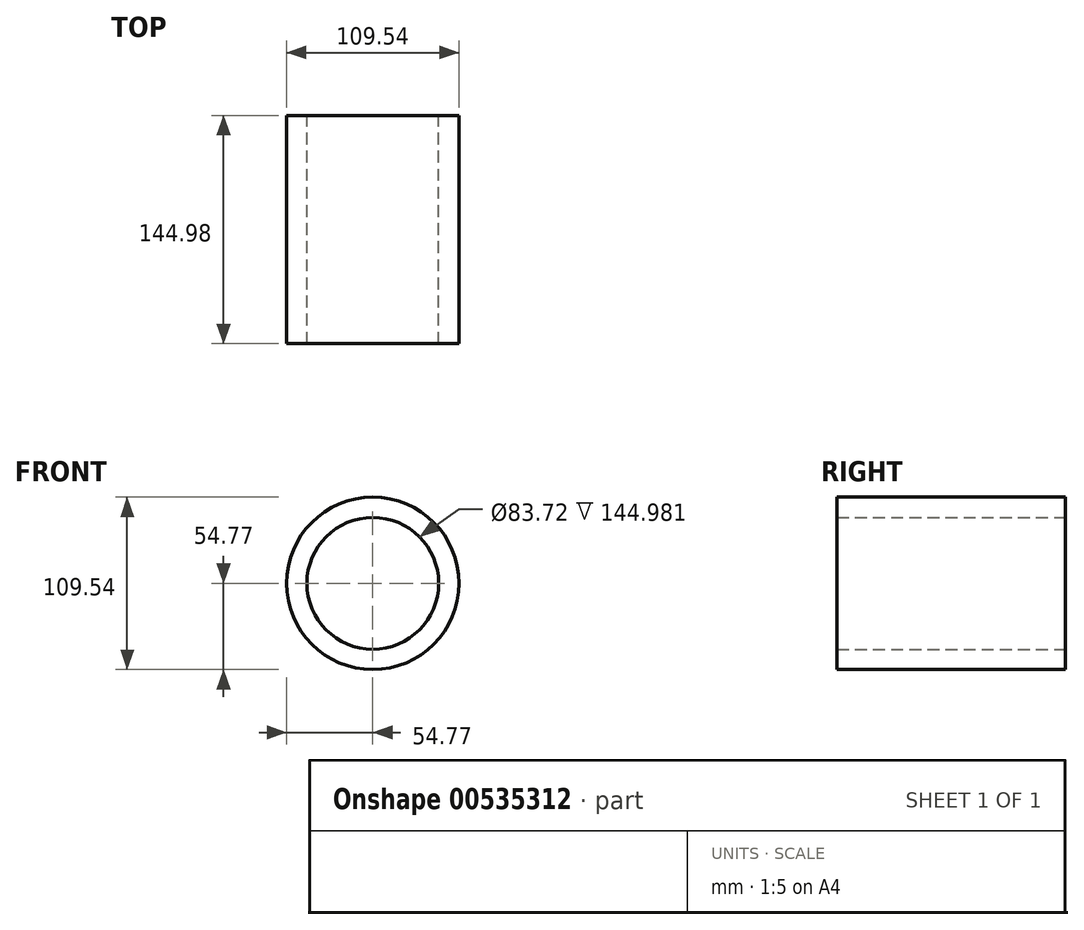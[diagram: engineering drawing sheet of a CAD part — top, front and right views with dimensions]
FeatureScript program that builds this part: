
annotation { "Feature Type Name" : "Feature", "Feature Type Description" : "" }
export const myFeature = defineFeature(function(context is Context, id is Id, definition is map)
    precondition{}
    {
        {
            var Q0;
            Q0=qCreatedBy(makeId("Front.planeOp"),FACE);
            var sketch = newSketch(context, id + "F0", { "sketchPlane" : qUnion([Q0])});
            skCircle(sketch, "E0", {"center": v(0, 0) * mm, "radius": 54.77 * mm});
            skCircle(sketch, "E1", {"center": v(0, 0) * mm, "radius": 41.86 * mm});
            skSolve(sketch);
        }
        {
            var Q0;
            Q0=makeQuery(id+"F0.imprint","IMPRINT",FACE,{"disambiguationData":[TD([[makeQuery(id+"F0.imprint","IMPRINT",EDGE,{"derivedFrom":sQuery(id+"F0.wireOp",EDGE,"E0")}),1.0]])]});
            extrude(context, id + "F1", {"entities" : qUnion([Q0]), "depth" : 144.98 * mm, "offsetDistance" : 25.4 * mm});
        }
    });
